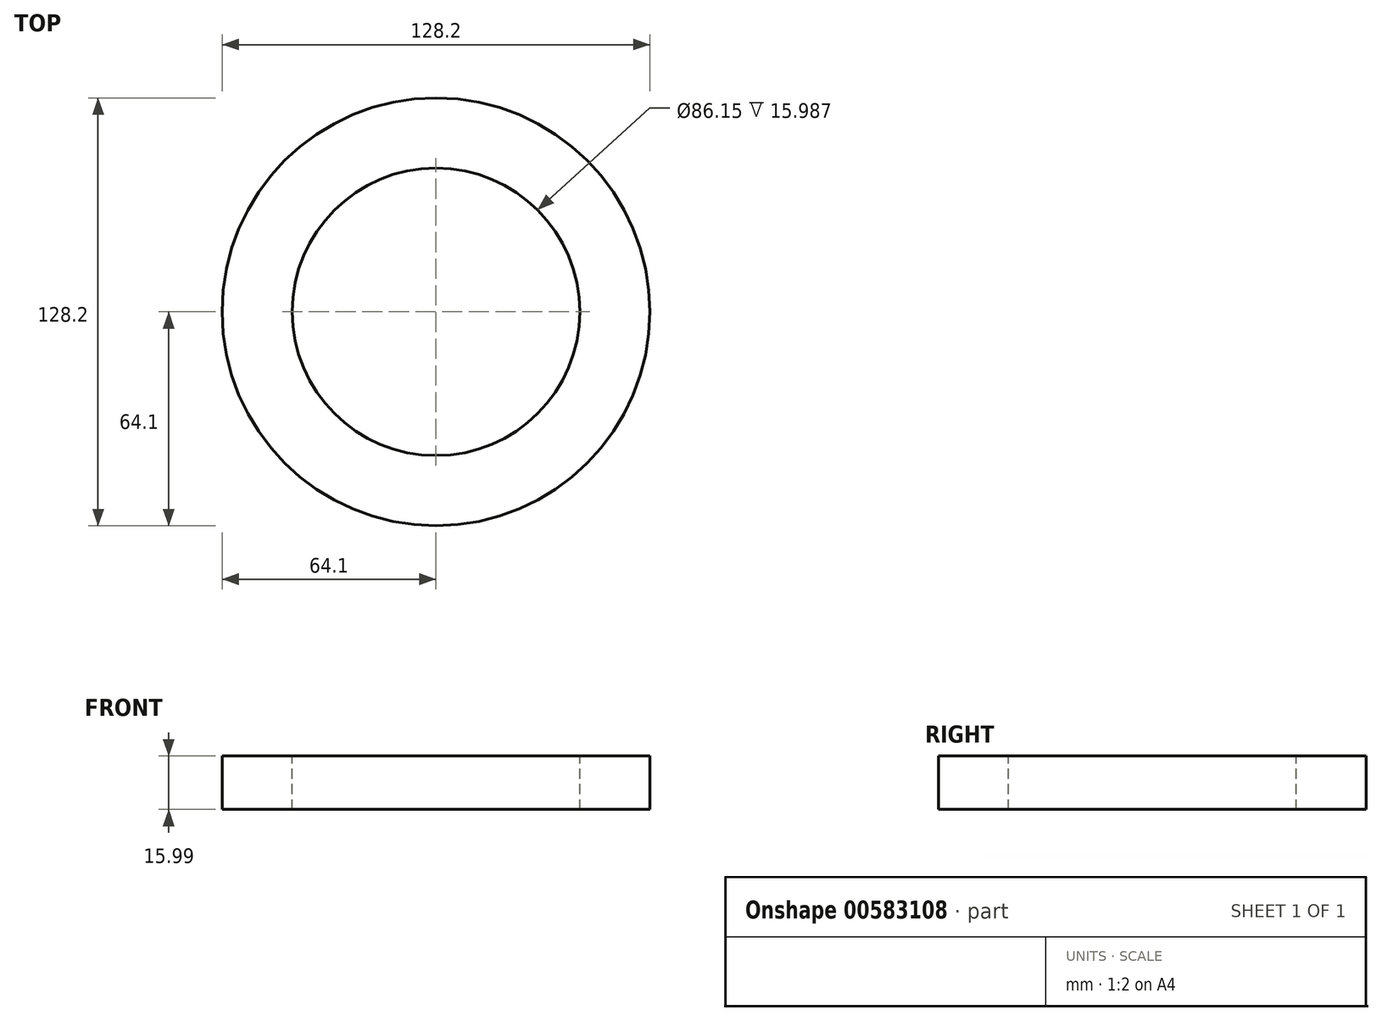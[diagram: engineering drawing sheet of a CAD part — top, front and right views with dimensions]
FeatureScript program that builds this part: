
annotation { "Feature Type Name" : "Feature", "Feature Type Description" : "" }
export const myFeature = defineFeature(function(context is Context, id is Id, definition is map)
    precondition{}
    {
        {
            var Q0;
            Q0=qCreatedBy(makeId("Front.planeOp"),FACE);
            var sketch = newSketch(context, id + "F0", { "sketchPlane" : qUnion([Q0])});
            skLineSegment(sketch, "E0", {"start": v(0, 64.69) * mm, "end": v(0, -40.12) * mm, "construction": true});
            skLineSegment(sketch, "E1.bottom", {"start": v(43.08, 41.9) * mm, "end": v(64.1, 41.9) * mm});
            skLineSegment(sketch, "E1.top", {"start": v(43.08, 25.9) * mm, "end": v(64.1, 25.9) * mm});
            skLineSegment(sketch, "E1.left", {"start": v(43.08, 41.9) * mm, "end": v(43.08, 25.9) * mm});
            skLineSegment(sketch, "E1.right", {"start": v(64.1, 41.9) * mm, "end": v(64.1, 25.9) * mm});
            skSolve(sketch);
        }
        {
            var Q0;
            Q0 = qSketchRegion(id + "F0", true);
            var Q1;
            Q1=sQuery(id+"F0.wireOp",EDGE,"E0");
            revolve(context, id + "F1", {"entities" : qUnion([Q0]), "axis" : qUnion([Q1]), "revolveType" : RevolveType.FULL});
        }
    });
